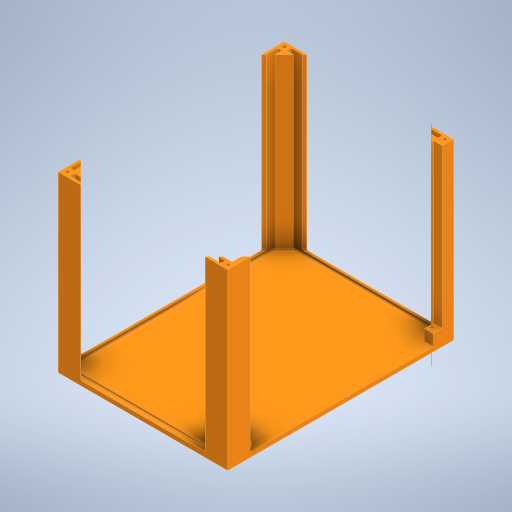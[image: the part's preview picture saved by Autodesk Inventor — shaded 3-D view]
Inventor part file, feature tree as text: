
AUTODESK INVENTOR PART (.ipt)
format: ipt  version: 2024.3 (Build 283343000, 343)  size: 427,008 bytes
history: native  units: mm
features: sketch x11, extrude x9, mirror x5, other x3, hole x2, fillet x1
ambient origin geometry x8: Origin, YZ Plane, XZ Plane, XY Plane, X Axis, Y Axis, Z Axis, Center Point
bodies: Body1 (feature_tree)
feature tree (31):
  other  "Těleso1"
  extrude  "Vysunutí1"  Depth=200.0mm
  extrude  "Vysunutí2"  Depth=150.0mm
  mirror  "Zrcadlit1"
  hole  "Díra1"  [1 undecoded]
  mirror  "Zrcadlit2"
  extrude  "Vysunutí3"  Depth=20.0mm
  mirror  "Zrcadlit3"
  other  "Pracovní rovina1"
  extrude  "Vysunutí6"  Depth=150.0mm TaperAngle=0.0deg
  mirror  "Zrcadlit4"
  extrude  "Vysunutí7"  Depth=2.0mm
  mirror  "Zrcadlit5"
  extrude  "Vysunutí8"  Depth=4.0mm
  extrude  "Vysunutí9"  Depth=10.0mm
  fillet  "Zaoblení1"  Radius=6.0mm
  extrude  "Vysunutí11"  Depth=8.0mm
  extrude  "Vysunutí12"  Depth=4.0mm
  hole  "Díra3"  [1 undecoded]
  other  "Pracovní osa1"
  sketch  "Náčrt1"
  sketch  "Náčrt2"
  sketch  "Náčrt3"
  sketch  "Náčrt4"
  sketch  "Náčrt7"
  sketch  "Náčrt9"
  sketch  "Náčrt10"
  sketch  "Náčrt11"
  sketch  "Náčrt13"
  sketch  "Náčrt14"
  sketch  "Náčrt15"
note: 2 required parameter values undecoded (feature->parameter linkage not recoverable at this tier; creation-order binding heuristic only, values carry confidence <= 0.55)
